# Revit family: ledapollo-e4_rd350-8_16w-dim-827_840_520033017500_484e
name_source: partatom
category: Lighting Fixtures
units: mm (PartAtom-declared; Revit-internal decimal feet)

## family parameters
Cut with Voids When Loaded = No
Host = Face
Light Source = No
Part Type = Normal
Room Calculation Point = No
Round Connector Dimension = Use Diameter
Shared = No

## types (1)
- LEDApollo-E4 Rd350-8/16W-DIM-827/840 (1 x LED, 1600 lm, 4000)
    Apparent Load = 8 VA
    Approval mark = CE
    CIE Flux Codes = 41 71 91 88 100
    Color Rendering = 80
    Color Temperature = 4000
    Control Gear = Electronic ballast
    Default Elevation = 1800 mm
    Description = Ceiling Light Apollo G4 Ø350mm-16W-800/1600lm2700/4000K-Triac
    Frequency = 60 Hz
    Height = 68 mm
    Lamp = 1 x LED
    Lamp Light Flux = 1600 lm
    Lamp count = 1
    Length = 350 mm
    Luminous efficacy = 200 lm/W
    Manufacturer = OPPLE
    ModVariant = No
    Model = 520033017500
    Number of Poles = 1
    OnlyDefault = Yes
    Power Factor = 1
    Product Name = LEDApollo-E4 Rd350-8/16W-DIM-827/840
    Product group = Ceiling / wall-mounted luminaires
    ProductGroupID = 30
    Protection Class = Protection class II
    Protection Degree = IP 44
    RLX_Detail_Level = 1
    RLX_Emergency_Light_Flux = 0 lm
    RLX_Emergency_Type = 0
    RLX_Emergency_Type_DB = No
    RlxData = <blob elided: 201737 chars, md5=12f7ff9f>
    Socket = socket
    Standby Power = 0 W
    System Light Flux = 1598 lm
    System Power = 8 W
    Type Comments = Product without accessories
    Type Image = web_apollo_e4.jpg
    URL = http://relux.com
    VarID = ---
    Voltage = 230 V
    Voltage Range = 220-240 V
    Weight = 0.00 kg
    Width = 350 mm

## geometry (parser evidence)
native form markers: Blend x4, Sweep x9
no freeform markers — native parametric forms only
